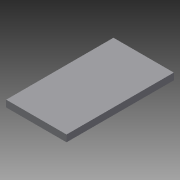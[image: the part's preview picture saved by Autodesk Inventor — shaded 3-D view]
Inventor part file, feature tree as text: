
AUTODESK INVENTOR PART (.ipt)
format: ipt  version: 2013 (Build 170138000, 138)  size: 67,072 bytes
history: native  units: in
note: dims shown in document units (in); Inventor stores cm internally (conversion verified against a paired STEP export)
features: extrude x1, sketch x1
ambient origin geometry x8: Origin, YZ Plane, XZ Plane, XY Plane, X Axis, Y Axis, Z Axis, Center Point
bodies: Solid1 (feature_tree)
feature tree (2):
  extrude  "Extrusion1"  Depth=0.125in TaperAngle=0.0deg
  sketch  "Sketch1"  dims[d0=1.125in d1=0.125in d2=0.0in d3=2.0in]
